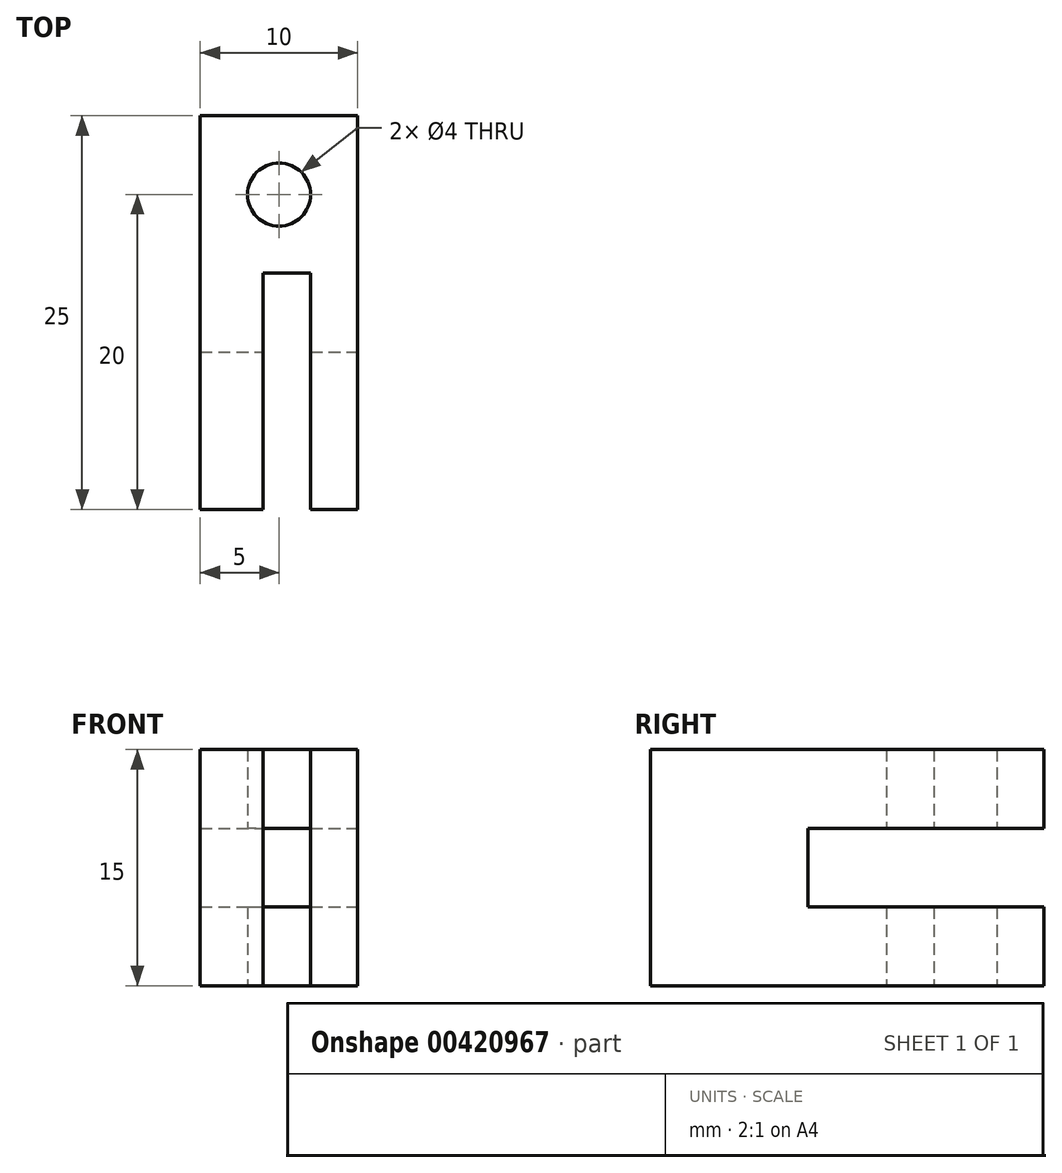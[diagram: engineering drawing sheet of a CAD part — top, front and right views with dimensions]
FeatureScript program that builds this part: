
annotation { "Feature Type Name" : "Feature", "Feature Type Description" : "" }
export const myFeature = defineFeature(function(context is Context, id is Id, definition is map)
    precondition{}
    {
        {
            var Q0;
            Q0=qCreatedBy(makeId("Top.planeOp"),FACE);
            var sketch = newSketch(context, id + "F0", { "sketchPlane" : qUnion([Q0])});
            skLineSegment(sketch, "E0", {"start": v(0, 0) * mm, "end": v(0, 15) * mm});
            skLineSegment(sketch, "E1", {"start": v(0, 15) * mm, "end": v(3, 15) * mm});
            skLineSegment(sketch, "E2", {"start": v(3, 15) * mm, "end": v(3, 0) * mm});
            skLineSegment(sketch, "E3", {"start": v(3, 0) * mm, "end": v(6, 0) * mm});
            skLineSegment(sketch, "E4", {"start": v(6, 0) * mm, "end": v(6, 25) * mm});
            skLineSegment(sketch, "E5", {"start": v(6, 25) * mm, "end": v(-4, 25) * mm});
            skLineSegment(sketch, "E6", {"start": v(-4, 25) * mm, "end": v(-4, 0) * mm});
            skLineSegment(sketch, "E7", {"start": v(-4, 0) * mm, "end": v(0, 0) * mm});
            skLineSegment(sketch, "E8", {"start": v(0, 0) * mm, "end": v(0, 0) * mm});
            skCircle(sketch, "E9", {"center": v(1, 20) * mm, "radius": 2 * mm});
            skSolve(sketch);
        }
        {
            var Q0;
            Q0=makeQuery(id+"F0.imprint","IMPRINT",FACE,{"disambiguationData":[TD([[makeQuery(id+"F0.imprint","IMPRINT",EDGE,{"derivedFrom":sQuery(id+"F0.wireOp",EDGE,"E0")}),1.0]])]});
            var Q1;
            Q1 = qSketchRegion(id + "F2", true);
            extrude(context, id + "F1", {"entities" : qUnion([Q0, Q1]), "depth" : 15 * mm});
        }
        {
            var Q0;
            Q0=makeQuery(id+"F1.opExtrude","SWEPT_FACE",FACE,{"disambiguationData":[OSD([sQuery(id+"F0.wireOp",EDGE,"E4")])]});
            var sketch = newSketch(context, id + "F2", { "sketchPlane" : qUnion([Q0])});
            skLineSegment(sketch, "E10", {"start": v(25, 10) * mm, "end": v(10, 10) * mm});
            skLineSegment(sketch, "E11", {"start": v(10, 10) * mm, "end": v(10, 5) * mm});
            skLineSegment(sketch, "E12", {"start": v(10, 5) * mm, "end": v(25, 5) * mm});
            skLineSegment(sketch, "E13", {"start": v(25, 5) * mm, "end": v(25, 10) * mm});
            skSolve(sketch);
        }
        {
            var Q0;
            Q0=makeQuery(id+"F2.imprint","IMPRINT",FACE,{"disambiguationData":[TD([[makeQuery(id+"F2.imprint","IMPRINT",EDGE,{"derivedFrom":sQuery(id+"F2.wireOp",EDGE,"E10")}),1.0]])]});
            extrude(context, id + "F3", {"entities" : qUnion([Q0]), "operationType" : NewBodyOperationType.REMOVE, "oppositeDirection" : true, "depth" : 25.4 * mm});
        }
    });
